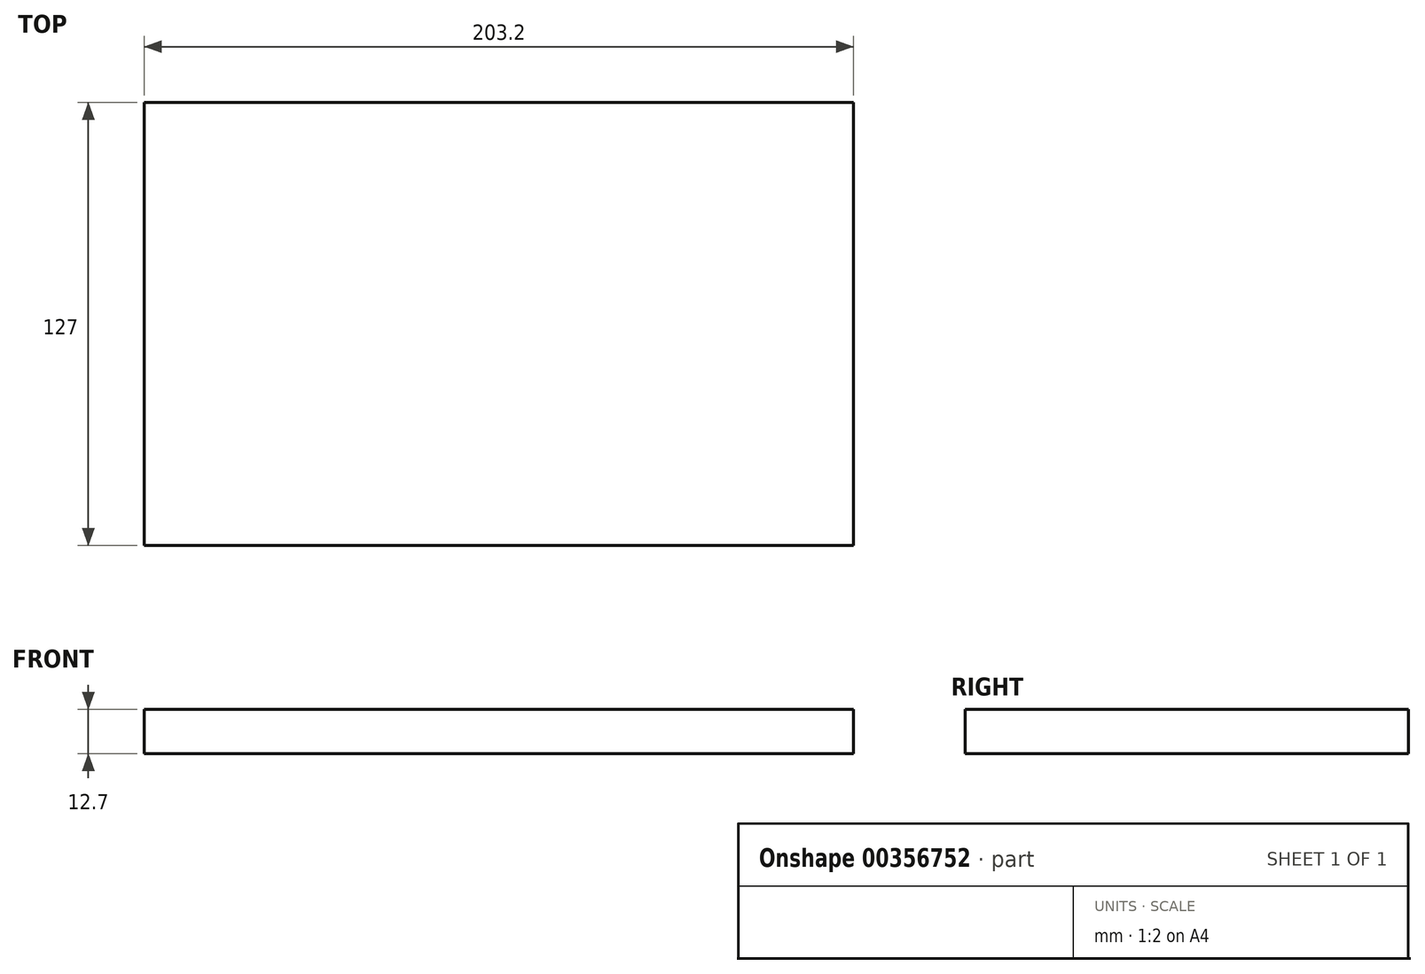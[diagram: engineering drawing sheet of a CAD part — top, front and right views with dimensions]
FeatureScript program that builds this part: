
annotation { "Feature Type Name" : "Feature", "Feature Type Description" : "" }
export const myFeature = defineFeature(function(context is Context, id is Id, definition is map)
    precondition{}
    {
        {
            var Q0;
            Q0=qCreatedBy(makeId("Top.planeOp"),FACE);
            var sketch = newSketch(context, id + "F0", { "sketchPlane" : qUnion([Q0])});
            skLineSegment(sketch, "E0.bottom", {"start": v(101.6, 63.5) * mm, "end": v(-101.6, 63.5) * mm});
            skLineSegment(sketch, "E0.top", {"start": v(101.6, -63.5) * mm, "end": v(-101.6, -63.5) * mm});
            skLineSegment(sketch, "E0.left", {"start": v(101.6, 63.5) * mm, "end": v(101.6, -63.5) * mm});
            skLineSegment(sketch, "E0.right", {"start": v(-101.6, 63.5) * mm, "end": v(-101.6, -63.5) * mm});
            skPoint(sketch, "E0.middle", {"position": v(0, 0) * mm});
            skSolve(sketch);
        }
        {
            var Q0;
            Q0 = qSketchRegion(id + "F0", true);
            extrude(context, id + "F1", {"entities" : qUnion([Q0]), "depth" : 12.7 * mm});
        }
    });
